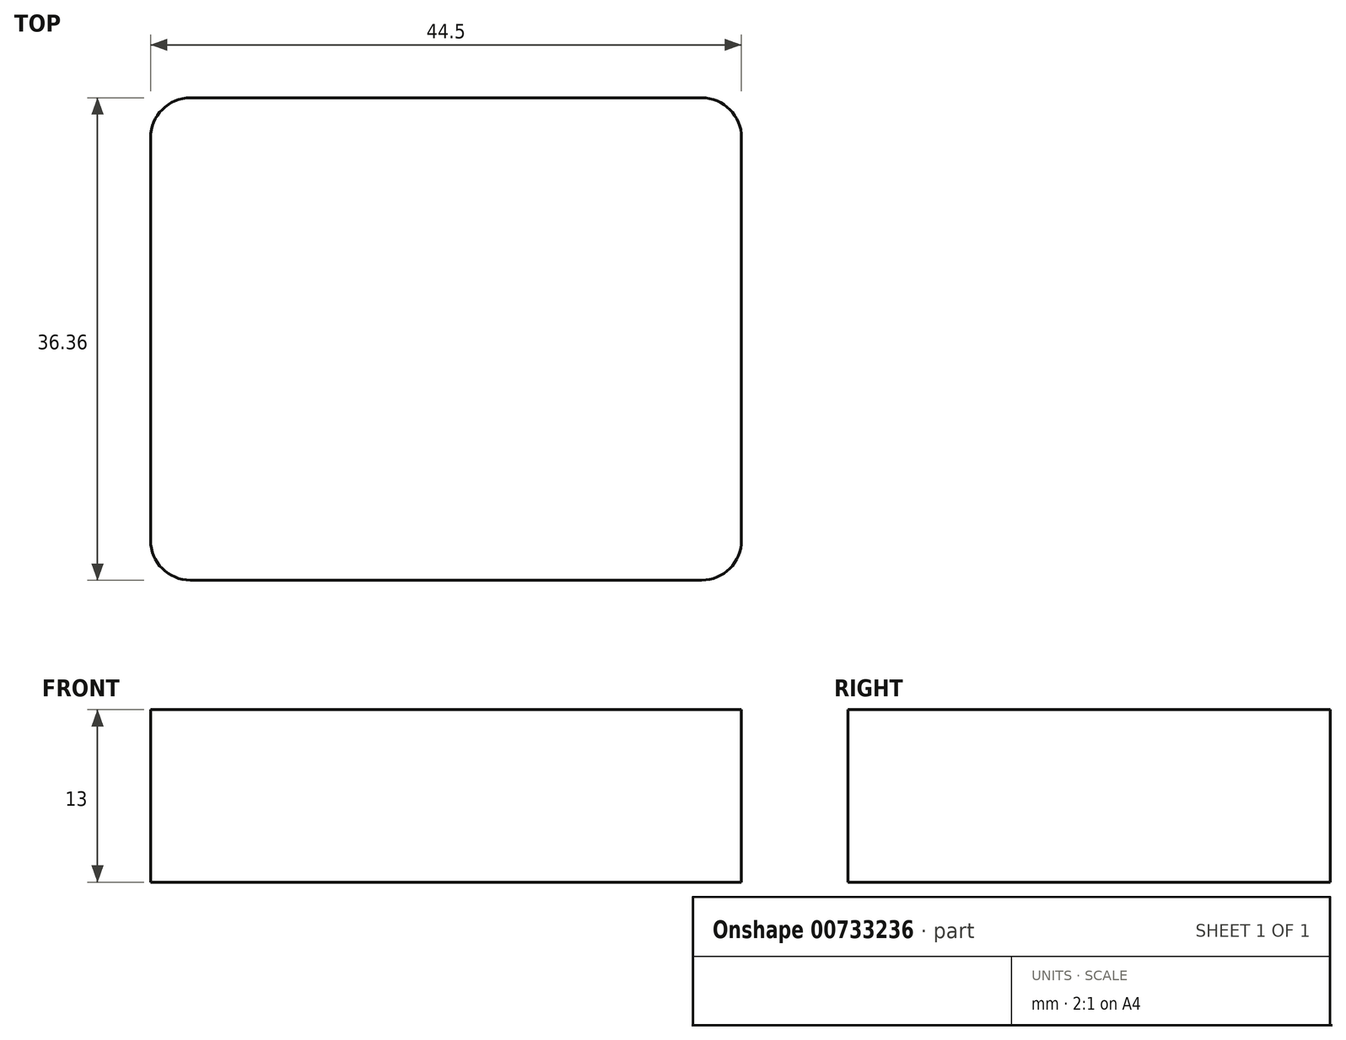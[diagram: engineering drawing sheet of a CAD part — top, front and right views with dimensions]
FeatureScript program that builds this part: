
annotation { "Feature Type Name" : "Feature", "Feature Type Description" : "" }
export const myFeature = defineFeature(function(context is Context, id is Id, definition is map)
    precondition{}
    {
        {
            var Q0;
            Q0=qCreatedBy(makeId("Top.planeOp"),FACE);
            var sketch = newSketch(context, id + "F0", { "sketchPlane" : qUnion([Q0])});
            skLineSegment(sketch, "E0.bottom", {"start": v(-19.25, 18.18) * mm, "end": v(19.25, 18.18) * mm});
            skLineSegment(sketch, "E0.top", {"start": v(-19.25, -18.18) * mm, "end": v(19.25, -18.18) * mm});
            skLineSegment(sketch, "E0.left", {"start": v(-22.25, 15.18) * mm, "end": v(-22.25, -15.18) * mm});
            skLineSegment(sketch, "E0.right", {"start": v(22.25, 15.18) * mm, "end": v(22.25, -15.18) * mm});
            skPoint(sketch, "E1.visualSharp", {"position": v(22.25, 18.18) * mm});
            skArc(sketch, "E1.filletArc", {"start": v(22.25, 15.18) * mm, "mid": v(21.37, 17.3) * mm, "end": v(19.25, 18.18) * mm});
            skPoint(sketch, "E2.visualSharp", {"position": v(-22.25, 18.18) * mm});
            skArc(sketch, "E2.filletArc", {"start": v(-19.25, 18.18) * mm, "mid": v(-21.37, 17.3) * mm, "end": v(-22.25, 15.18) * mm});
            skPoint(sketch, "E3.visualSharp", {"position": v(-22.25, -18.18) * mm});
            skArc(sketch, "E3.filletArc", {"start": v(-22.25, -15.18) * mm, "mid": v(-21.37, -17.3) * mm, "end": v(-19.25, -18.18) * mm});
            skPoint(sketch, "E4.visualSharp", {"position": v(22.25, -18.18) * mm});
            skArc(sketch, "E4.filletArc", {"start": v(19.25, -18.18) * mm, "mid": v(21.37, -17.3) * mm, "end": v(22.25, -15.18) * mm});
            skSolve(sketch);
        }
        {
            var Q0;
            Q0=makeQuery(id+"F0.imprint","IMPRINT",FACE,{"disambiguationData":[TD([[makeQuery(id+"F0.imprint","IMPRINT",EDGE,{"derivedFrom":sQuery(id+"F0.wireOp",EDGE,"E0.bottom")}),-1.0]])]});
            extrude(context, id + "F1", {"entities" : qUnion([Q0]), "depth" : 13 * mm, "offsetDistance" : 25 * mm});
        }
    });
